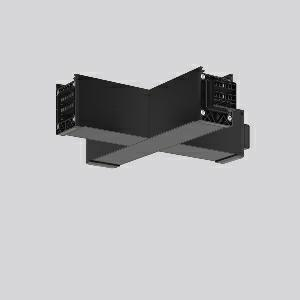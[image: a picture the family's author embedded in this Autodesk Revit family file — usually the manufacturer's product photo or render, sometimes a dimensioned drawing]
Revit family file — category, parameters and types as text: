
# Revit family: linedo_x-verbindung_982775_003_6ed3
name_source: partatom
category: Lighting Fixtures
units: mm (PartAtom-declared; Revit-internal decimal feet)

## family parameters
Cut with Voids When Loaded = No
Host = Face
Light Source = No
Part Type = Normal
Room Calculation Point = No
Round Connector Dimension = Use Diameter
Shared = No

## types (1)
- LINEDO X-Verbindung
    Apparent Load = 0 VA
    Default Elevation = 1800 mm
    Description = Series: LINEDO
X-connector, 14-pole, connection plug / socket / plug / socket. Housing: extruded aluminium profile, powder-coated. Cover made of plastic, surface like housing. LINEDO plug system, plastic, black. Easy connection for rigid or flexible wires. 6 membrane cable entries (2 x M20 and 4 x M25). Suitable for power supply in 7-pole version. Ready prewired. Colour-coded individual cables enable easy electromechanical separation.
Colour: jet black (RAL 9005)
Length: 330 mm
Width: 330 mm
Height: 76 mm
Weight: 1410 g
    Height = 76 mm
    Lamp = 0 x
    Length = 331 mm
    Luminous efficacy = 0 lm/W
    Manufacturer = RZB
    ModVariant = No
    Model = 982775.003
    Mounting Place = Ceiling
    Mounting Type = Surface mounted
    Number of Poles = 1
    OnlyDefault = Yes
    Power Factor = 1
    Product Name = LINEDO X-Verbindung
    Product group = Surface mounted continuous line luminaire system
    ProductGroupID = 310
    Protection Class = Protection class I
    Protection Degree = Degree of protection
    RLX_Detail_Level = 1
    RLX_Emergency_Light_Flux = 0 lm
    RLX_Emergency_Type = 0
    RLX_Emergency_Type_DB = No
    RlxData = <blob elided: 22773 chars, md5=5ac38d78>
    Standby Power = 0 W
    System Light Flux = 0 lm
    System Power = 0 W
    Type Comments = Product without accessories
    Type Image = 982775.003.jpg
    URL = http://relux.com
    VarID = ---
    Voltage = 0 V
    Weight = 0.00 kg
    Width = 331 mm

## geometry (parser evidence)
native form markers: Blend x4, Sweep x10
no freeform markers — native parametric forms only
